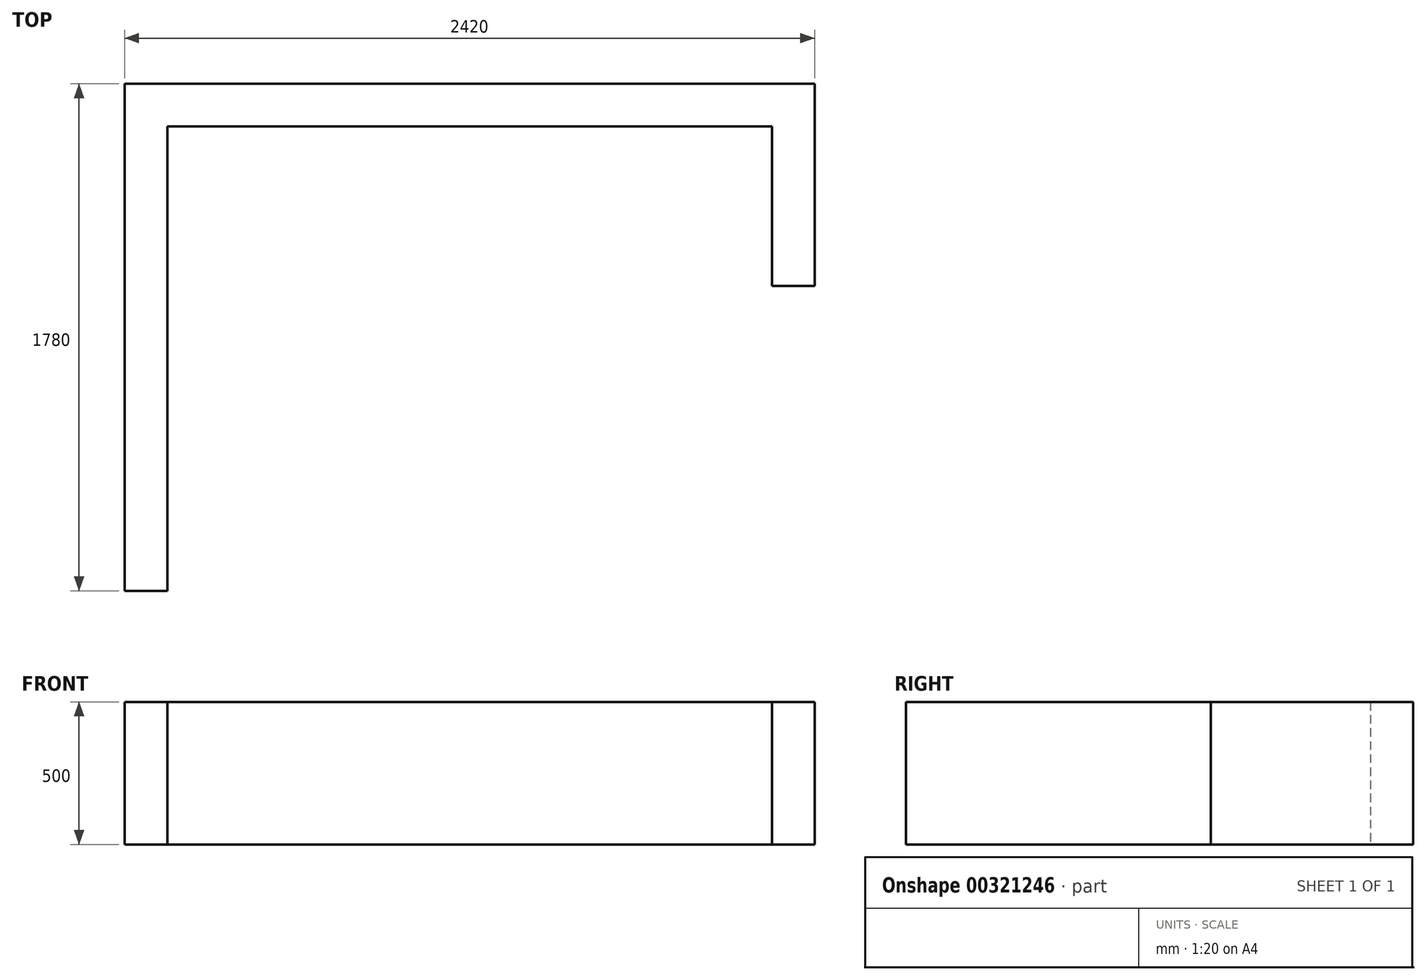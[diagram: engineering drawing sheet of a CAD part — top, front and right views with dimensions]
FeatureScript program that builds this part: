
annotation { "Feature Type Name" : "Feature", "Feature Type Description" : "" }
export const myFeature = defineFeature(function(context is Context, id is Id, definition is map)
    precondition{}
    {
        {
            var Q0;
            Q0=qCreatedBy(makeId("Top.planeOp"),FACE);
            var sketch = newSketch(context, id + "F0", { "sketchPlane" : qUnion([Q0])});
            skLineSegment(sketch, "E0", {"start": v(0, 0) * mm, "end": v(0, 1630) * mm});
            skLineSegment(sketch, "E1", {"start": v(0, 1630) * mm, "end": v(2120, 1630) * mm});
            skLineSegment(sketch, "E2", {"start": v(2120, 1630) * mm, "end": v(2120, 1070) * mm});
            skLineSegment(sketch, "E3", {"start": v(2120, 1070) * mm, "end": v(2270, 1070) * mm});
            skLineSegment(sketch, "E4", {"start": v(2270, 1070) * mm, "end": v(2270, 1780) * mm});
            skLineSegment(sketch, "E5", {"start": v(2270, 1780) * mm, "end": v(-150, 1780) * mm});
            skLineSegment(sketch, "E6", {"start": v(-150, 1780) * mm, "end": v(-150, 0) * mm});
            skLineSegment(sketch, "E7", {"start": v(-150, 0) * mm, "end": v(0, 0) * mm});
            skSolve(sketch);
        }
        {
            var Q0;
            Q0 = qSketchRegion(id + "F0", true);
            extrude(context, id + "F1", {"entities" : qUnion([Q0]), "depth" : 500 * mm});
        }
    });
